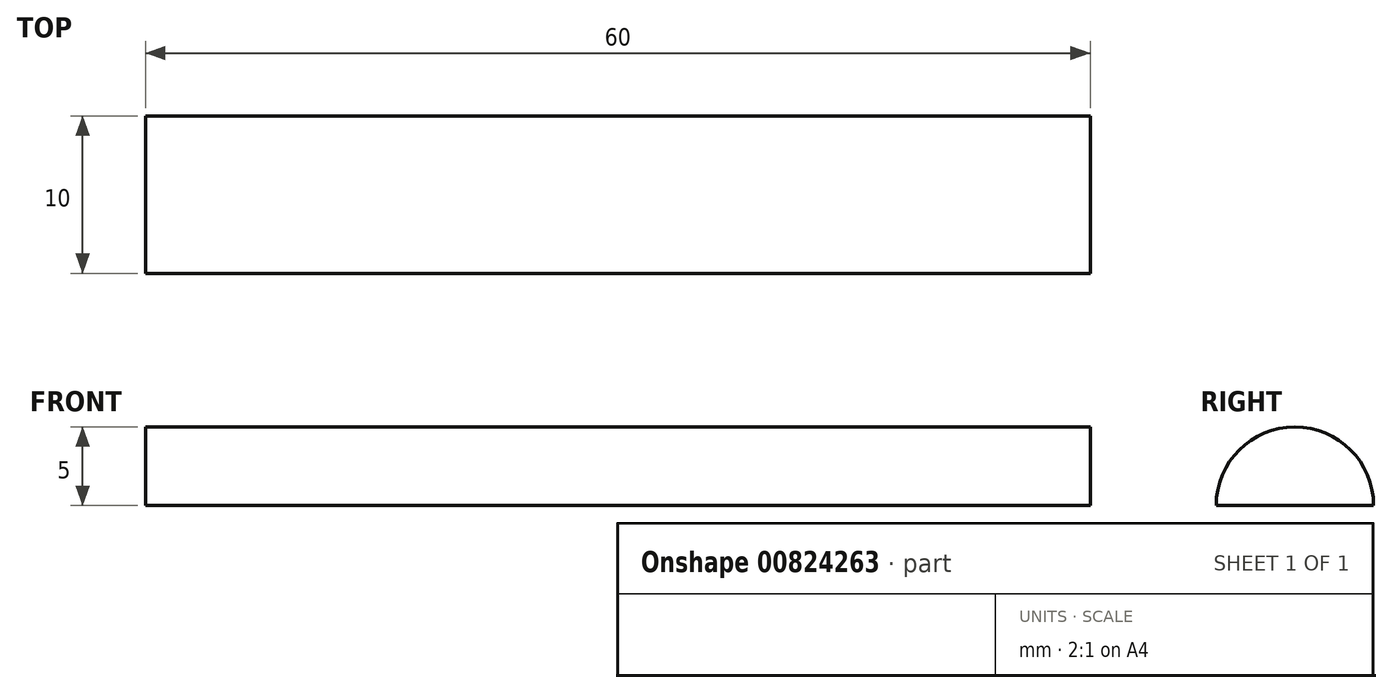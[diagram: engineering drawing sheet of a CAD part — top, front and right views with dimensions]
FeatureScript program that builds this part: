
annotation { "Feature Type Name" : "Feature", "Feature Type Description" : "" }
export const myFeature = defineFeature(function(context is Context, id is Id, definition is map)
    precondition{}
    {
        {
            var Q0;
            Q0=qCreatedBy(makeId("Right.planeOp"),FACE);
            var sketch = newSketch(context, id + "F0", { "sketchPlane" : qUnion([Q0])});
            skArc(sketch, "E0", {"start": v(5, 0) * mm, "mid": v(0, 5) * mm, "end": v(-5, 0) * mm});
            skLineSegment(sketch, "E1", {"start": v(-5, 0) * mm, "end": v(5, 0) * mm});
            skSolve(sketch);
        }
        {
            var Q0;
            Q0=makeQuery(id+"F0.imprint","IMPRINT",FACE,{"disambiguationData":[TD([[makeQuery(id+"F0.imprint","IMPRINT",EDGE,{"derivedFrom":sQuery(id+"F0.wireOp",EDGE,"E0")}),1.0]])]});
            extrude(context, id + "F1", {"entities" : qUnion([Q0]), "depth" : 60 * mm, "offsetDistance" : 25 * mm});
        }
    });
